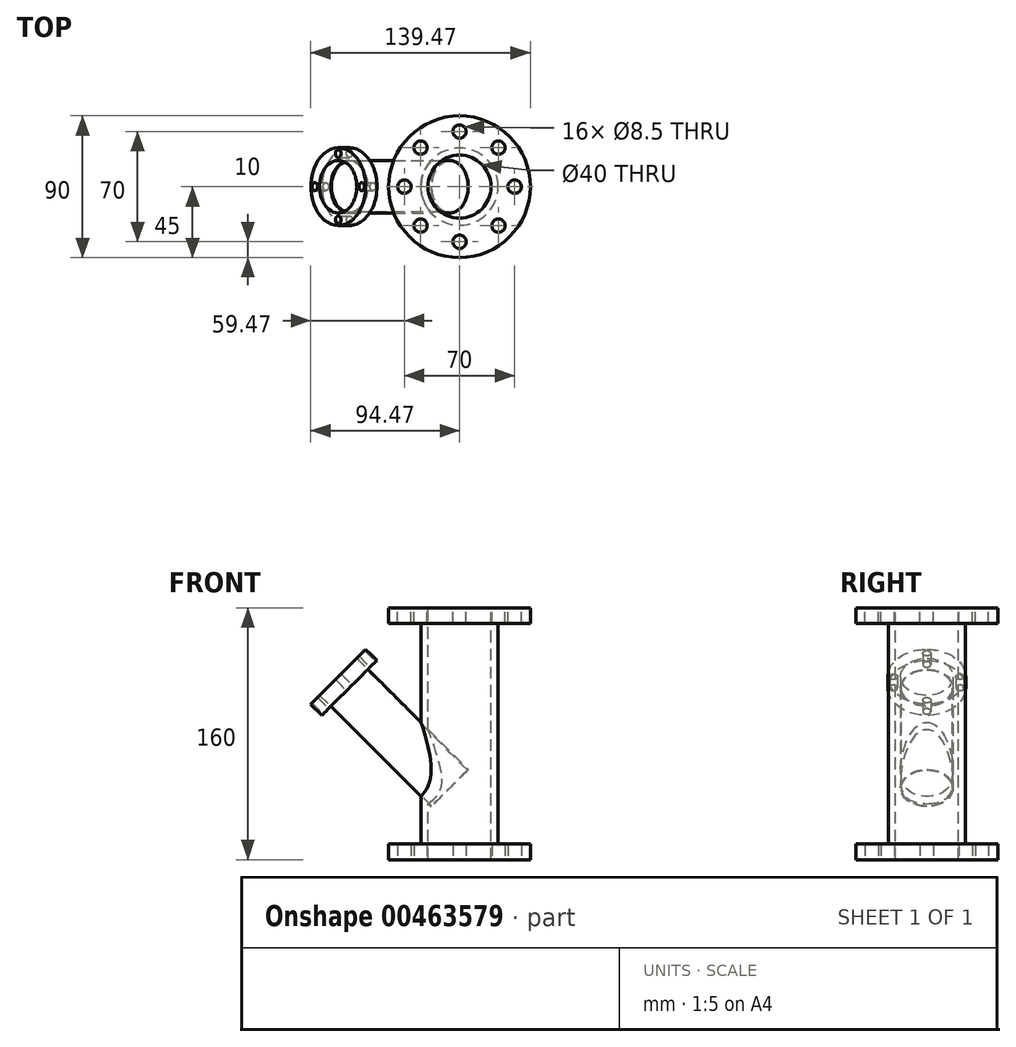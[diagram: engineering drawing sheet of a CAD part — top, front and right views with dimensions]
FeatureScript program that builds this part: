
annotation { "Feature Type Name" : "Feature", "Feature Type Description" : "" }
export const myFeature = defineFeature(function(context is Context, id is Id, definition is map)
    precondition{}
    {
        {
            var Q0;
            Q0=qCreatedBy(makeId("Top.planeOp"),FACE);
            var sketch = newSketch(context, id + "F0", { "sketchPlane" : qUnion([Q0])});
            skCircle(sketch, "E0", {"center": v(0, 0) * mm, "radius": 45 * mm});
            skSolve(sketch);
        }
        {
            var Q0;
            Q0=makeQuery(id+"F0.imprint","IMPRINT",FACE,{"disambiguationData":[TD([[makeQuery(id+"F0.imprint","IMPRINT",EDGE,{"derivedFrom":sQuery(id+"F0.wireOp",EDGE,"E0")}),1.0]])]});
            extrude(context, id + "F1", {"entities" : qUnion([Q0]), "depth" : 10 * mm});
        }
        {
            var Q0;
            Q0=makeQuery(id+"F1.opExtrude","CAP_FACE",FACE,{"disambiguationData":[OSD([sQuery(id+"F0.wireOp",EDGE,"E0")])],"isStart":true});
            var sketch = newSketch(context, id + "F2", { "sketchPlane" : qUnion([Q0])});
            skCircle(sketch, "E1", {"center": v(0, 0) * mm, "radius": 35 * mm});
            skCircle(sketch, "E2", {"center": v(0, 0) * mm, "radius": 20 * mm});
            skSolve(sketch);
        }
        {
            var Q0;
            Q0=makeQuery(id+"F1.opExtrude","CAP_FACE",FACE,{"disambiguationData":[OSD([sQuery(id+"F0.wireOp",EDGE,"E0")])],"isStart":false});
            var sketch = newSketch(context, id + "F3", { "sketchPlane" : qUnion([Q0])});
            skCircle(sketch, "E3", {"center": v(0, 0) * mm, "radius": 24.5 * mm});
            skSolve(sketch);
        }
        {
            var Q0;
            Q0=makeQuery(id+"F3.imprint","IMPRINT",FACE,{"disambiguationData":[TD([[makeQuery(id+"F3.imprint","IMPRINT",EDGE,{"derivedFrom":sQuery(id+"F3.wireOp",EDGE,"E3")}),1.0]])]});
            extrude(context, id + "F4", {"entities" : qUnion([Q0]), "operationType" : NewBodyOperationType.ADD, "depth" : 140 * mm});
        }
        {
            var Q0;
            Q0=makeQuery(id+"F4.opExtrude","CAP_FACE",FACE,{"disambiguationData":[OSD([sQuery(id+"F3.wireOp",EDGE,"E3")])],"isStart":false});
            var sketch = newSketch(context, id + "F5", { "sketchPlane" : qUnion([Q0])});
            skCircle(sketch, "E4", {"center": v(0, 0) * mm, "radius": 45 * mm});
            skSolve(sketch);
        }
        {
            var Q0;
            Q0=makeQuery(id+"F5.imprint","IMPRINT",FACE,{"disambiguationData":[TD([[makeQuery(id+"F5.imprint","IMPRINT",EDGE,{"derivedFrom":sQuery(id+"F5.wireOp",EDGE,"E4")}),1.0]])]});
            var Q1;
            Q1=makeQuery(id+"F5.imprint","IMPRINT",FACE,{"disambiguationData":[TD([[makeQuery(id+"F5.imprint","IMPRINT",EDGE,{"derivedFrom":makeQuery(id+"F4.opExtrude","CAP_EDGE",EDGE,{"disambiguationData":[OSD([sQuery(id+"F3.wireOp",EDGE,"E3")])],"isStart":false})}),1.0]])]});
            extrude(context, id + "F6", {"entities" : qUnion([Q0, Q1]), "operationType" : NewBodyOperationType.ADD, "depth" : 10 * mm});
        }
        {
            var Q0;
            Q0=makeQuery(id+"F6.opExtrude","CAP_FACE",FACE,{"disambiguationData":[OSD([sQuery(id+"F5.wireOp",EDGE,"E4")])],"isStart":false});
            var sketch = newSketch(context, id + "F7", { "sketchPlane" : qUnion([Q0])});
            skCircle(sketch, "E5", {"center": v(0, 0) * mm, "radius": 20 * mm});
            skCircle(sketch, "E6", {"center": v(0, 0) * mm, "radius": 35 * mm});
            skSolve(sketch);
        }
        {
            var Q0;
            Q0=makeQuery(id+"F7.imprint","IMPRINT",FACE,{"disambiguationData":[TD([[makeQuery(id+"F7.imprint","IMPRINT",EDGE,{"derivedFrom":sQuery(id+"F7.wireOp",EDGE,"E5")}),1.0]])]});
            extrude(context, id + "F8", {"entities" : qUnion([Q0]), "operationType" : NewBodyOperationType.REMOVE, "oppositeDirection" : true, "depth" : 500 * mm});
        }
        {
            var Q0;
            Q0=makeQuery(id+"F2.imprint","IMPRINT",FACE,{"disambiguationData":[TD([[makeQuery(id+"F2.imprint","IMPRINT",EDGE,{"derivedFrom":sQuery(id+"F2.wireOp",EDGE,"E1")}),-1.0]])]});
            var sketch = newSketch(context, id + "F9", { "sketchPlane" : qUnion([Q0])});
            skLineSegment(sketch, "E7", {"start": v(0, 0) * mm, "end": v(0, 30.75) * mm});
            skLineSegment(sketch, "E8", {"start": v(0, 75.16) * mm, "end": v(0, 39.25) * mm});
            skLineSegment(sketch, "E9", {"start": v(0, 0) * mm, "end": v(30.75, 0) * mm});
            skLineSegment(sketch, "E10", {"start": v(92.22, 0) * mm, "end": v(39.25, 0) * mm});
            skLineSegment(sketch, "E11", {"start": v(0, 0) * mm, "end": v(21.74, 21.74) * mm});
            skLineSegment(sketch, "E12", {"start": v(58.34, 58.34) * mm, "end": v(27.75, 27.75) * mm});
            skLineSegment(sketch, "E13", {"start": v(0, 0) * mm, "end": v(-60.15, 60.15) * mm});
            skLineSegment(sketch, "E14", {"start": v(-60.15, 60.15) * mm, "end": v(-27.75, 27.75) * mm});
            skArc(sketch, "E15", {"start": v(-27.57, 21.57) * mm, "mid": v(-32.34, 13.4) * mm, "end": v(-34.74, 4.24) * mm});
            skCircle(sketch, "E16", {"center": v(35, 0) * mm, "radius": 4.25 * mm});
            skCircle(sketch, "E17", {"center": v(24.75, 24.75) * mm, "radius": 4.25 * mm});
            skCircle(sketch, "E18", {"center": v(0, 35) * mm, "radius": 4.25 * mm});
            skCircle(sketch, "E19", {"center": v(24.75, -24.75) * mm, "radius": 4.25 * mm});
            skCircle(sketch, "E20", {"center": v(0, -35) * mm, "radius": 4.25 * mm});
            skCircle(sketch, "E21", {"center": v(-24.75, -24.75) * mm, "radius": 4.25 * mm});
            skCircle(sketch, "E22", {"center": v(-35, 0) * mm, "radius": 4.25 * mm});
            skCircle(sketch, "E23", {"center": v(-24.75, 24.75) * mm, "radius": 4.25 * mm});
            skLineSegment(sketch, "E24.trimOffspring", {"start": v(-21.74, 21.74) * mm, "end": v(21.74, -21.74) * mm});
            skLineSegment(sketch, "E25.trimOffspring", {"start": v(0, 30.75) * mm, "end": v(0, -30.75) * mm});
            skLineSegment(sketch, "E26.trimOffspring", {"start": v(0, 39.25) * mm, "end": v(0, 75.16) * mm});
            skArc(sketch, "E27.trimOffspring", {"start": v(21.57, 27.57) * mm, "mid": v(13.4, 32.34) * mm, "end": v(4.24, 34.74) * mm});
            skLineSegment(sketch, "E28.trimOffspring", {"start": v(21.74, 21.74) * mm, "end": v(0, 0) * mm});
            skLineSegment(sketch, "E29.trimOffspring", {"start": v(27.75, 27.75) * mm, "end": v(58.34, 58.34) * mm});
            skLineSegment(sketch, "E30.trimOffspring", {"start": v(30.75, 0) * mm, "end": v(0, 0) * mm});
            skLineSegment(sketch, "E31.trimOffspring", {"start": v(39.25, 0) * mm, "end": v(92.22, 0) * mm});
            skArc(sketch, "E32.trimOffspring", {"start": v(34.74, 4.24) * mm, "mid": v(32.34, 13.4) * mm, "end": v(27.57, 21.57) * mm});
            skLineSegment(sketch, "E33.trimOffspring", {"start": v(27.75, -27.75) * mm, "end": v(66.62, -66.62) * mm});
            skArc(sketch, "E34.trimOffspring", {"start": v(27.57, -21.57) * mm, "mid": v(32.34, -13.4) * mm, "end": v(34.74, -4.24) * mm});
            skArc(sketch, "E35.trimOffspring", {"start": v(4.24, -34.74) * mm, "mid": v(13.4, -32.34) * mm, "end": v(21.57, -27.57) * mm});
            skLineSegment(sketch, "E36.trimOffspring", {"start": v(0, -39.25) * mm, "end": v(0, -74.56) * mm});
            skArc(sketch, "E37.trimOffspring", {"start": v(-21.57, -27.57) * mm, "mid": v(-13.4, -32.34) * mm, "end": v(-4.24, -34.74) * mm});
            skLineSegment(sketch, "E38.trimOffspring", {"start": v(-27.75, -27.75) * mm, "end": v(-65.53, -65.53) * mm});
            skArc(sketch, "E39.trimOffspring", {"start": v(-34.74, -4.24) * mm, "mid": v(-32.34, -13.4) * mm, "end": v(-27.57, -21.57) * mm});
            skLineSegment(sketch, "E40.trimOffspring", {"start": v(-39.25, 0) * mm, "end": v(-107.6, 0) * mm});
            skSolve(sketch);
        }
        {
            var Q0;
            Q0=sQuery(id+"F9.wireOp",VERTEX,"E18.center");
            var Q1;
            Q1=sQuery(id+"F9.wireOp",VERTEX,"E17.center");
            var Q2;
            Q2=sQuery(id+"F9.wireOp",VERTEX,"E16.center");
            var Q3;
            Q3=sQuery(id+"F9.wireOp",VERTEX,"E19.center");
            var Q4;
            Q4=sQuery(id+"F9.wireOp",VERTEX,"E20.center");
            var Q5;
            Q5=sQuery(id+"F9.wireOp",VERTEX,"E21.center");
            var Q6;
            Q6=sQuery(id+"F9.wireOp",VERTEX,"E22.center");
            var Q7;
            Q7=sQuery(id+"F9.wireOp",VERTEX,"E23.center");
            var Q8;
            Q8=makeQuery(id+"F1.opExtrude","SWEPT_BODY",BODY,{"disambiguationData":[OSD([sQuery(id+"F0.wireOp",EDGE,"E0")])]});
            hole(context, id + "F10", {"style" : HoleStyle.SIMPLE, "endStyle" : HoleEndStyle.BLIND, "holeDiameter" : 8.5 * mm, "holeDepth" : 11 * mm, "isTappedThrough" : true, "tappedDepth" : 12 * mm, "tapClearance" : 3, "startFromSketch" : true, "locations" : qUnion([Q0, Q1, Q2, Q3, Q4, Q5, Q6, Q7]), "scope" : qUnion([Q8])});
        }
        {
            var Q0;
            Q0=makeQuery(id+"F6.opExtrude","CAP_FACE",FACE,{"disambiguationData":[OSD([sQuery(id+"F5.wireOp",EDGE,"E4")])],"isStart":false});
            var sketch = newSketch(context, id + "F11", { "sketchPlane" : qUnion([Q0])});
            skLineSegment(sketch, "E41", {"start": v(0, 0) * mm, "end": v(0, 45) * mm});
            skLineSegment(sketch, "E42", {"start": v(0, 45) * mm, "end": v(0, -45) * mm});
            skLineSegment(sketch, "E43", {"start": v(0, 0) * mm, "end": v(45, 0) * mm});
            skLineSegment(sketch, "E44", {"start": v(0, 0) * mm, "end": v(-45, 0) * mm});
            skLineSegment(sketch, "E45", {"start": v(0, 0) * mm, "end": v(45.49, 45.49) * mm});
            skLineSegment(sketch, "E46", {"start": v(0, 0) * mm, "end": v(-38.13, 38.13) * mm});
            skLineSegment(sketch, "E47", {"start": v(-38.13, 38.13) * mm, "end": v(51.85, -51.85) * mm});
            skLineSegment(sketch, "E48", {"start": v(45.49, 45.49) * mm, "end": v(-48.36, -48.36) * mm});
            skCircle(sketch, "E49", {"center": v(0, 0) * mm, "radius": 35 * mm});
            skCircle(sketch, "E50", {"center": v(-24.75, 24.75) * mm, "radius": 7.46 * mm});
            skCircle(sketch, "E51", {"center": v(0, 35) * mm, "radius": 6.7 * mm});
            skCircle(sketch, "E52", {"center": v(24.75, 24.75) * mm, "radius": 4.32 * mm});
            skCircle(sketch, "E53", {"center": v(35, 0) * mm, "radius": 2.12 * mm});
            skCircle(sketch, "E54", {"center": v(24.75, -24.75) * mm, "radius": 4.97 * mm});
            skCircle(sketch, "E55", {"center": v(0, -35) * mm, "radius": 4.88 * mm});
            skCircle(sketch, "E56", {"center": v(-24.75, -24.75) * mm, "radius": 2.86 * mm});
            skCircle(sketch, "E57", {"center": v(-35, 0) * mm, "radius": 1.96 * mm});
            skSolve(sketch);
        }
        {
            var Q0;
            Q0=sQuery(id+"F11.wireOp",VERTEX,"E50.center");
            var Q1;
            Q1=sQuery(id+"F11.wireOp",VERTEX,"E51.center");
            var Q2;
            Q2=sQuery(id+"F11.wireOp",VERTEX,"E52.center");
            var Q3;
            Q3=sQuery(id+"F11.wireOp",VERTEX,"E53.center");
            var Q4;
            Q4=sQuery(id+"F11.wireOp",VERTEX,"E54.center");
            var Q5;
            Q5=sQuery(id+"F11.wireOp",VERTEX,"E55.center");
            var Q6;
            Q6=sQuery(id+"F11.wireOp",VERTEX,"E56.center");
            var Q7;
            Q7=sQuery(id+"F11.wireOp",VERTEX,"E57.center");
            var Q8;
            Q8=makeQuery(id+"F1.opExtrude","SWEPT_BODY",BODY,{"disambiguationData":[OSD([sQuery(id+"F0.wireOp",EDGE,"E0")])]});
            hole(context, id + "F12", {"style" : HoleStyle.SIMPLE, "endStyle" : HoleEndStyle.BLIND, "holeDiameter" : 8.5 * mm, "holeDepth" : 11 * mm, "isTappedThrough" : true, "tappedDepth" : 12 * mm, "tapClearance" : 3, "startFromSketch" : true, "locations" : qUnion([Q0, Q1, Q2, Q3, Q4, Q5, Q6, Q7]), "scope" : qUnion([Q8])});
        }
        {
            var Q0;
            Q0=qCreatedBy(makeId("Front.planeOp"),FACE);
            var sketch = newSketch(context, id + "F13", { "sketchPlane" : qUnion([Q0])});
            skLineSegment(sketch, "E58", {"start": v(0, 0) * mm, "end": v(0, 120.53) * mm});
            skLineSegment(sketch, "E59", {"start": v(0, 0) * mm, "end": v(0, 40) * mm});
            skLineSegment(sketch, "E60", {"start": v(0, 40) * mm, "end": v(-75.44, 115.44) * mm});
            skSolve(sketch);
        }
        {
            var Q0;
            Q0=sQuery(id+"F13.wireOp",EDGE,"E60");
            cPlane(context, id + "F14", {"entities" : qUnion([Q0]), "cplaneType" : CPlaneType.MID_PLANE, "offset" : 25 * mm, "width" : 150 * mm, "height" : 150 * mm});
        }
        {
            var Q0;
            Q0=qCreatedBy(id+"F14.planeOp",FACE);
            var sketch = newSketch(context, id + "F15", { "sketchPlane" : qUnion([Q0])});
            skCircle(sketch, "E61", {"center": v(0, 27.71) * mm, "radius": 16.68 * mm});
            skSolve(sketch);
        }
        {
            var Q0;
            Q0=makeQuery(id+"F15.imprint","IMPRINT",FACE,{"disambiguationData":[TD([[makeQuery(id+"F15.imprint","IMPRINT",EDGE,{"derivedFrom":sQuery(id+"F15.wireOp",EDGE,"E61")}),1.0]])]});
            extrude(context, id + "F16", {"entities" : qUnion([Q0]), "operationType" : NewBodyOperationType.ADD, "endBound" : BoundingType.SYMMETRIC, "depth" : 90 * mm});
        }
        {
            var Q0;
            Q0=makeQuery(id+"F16.opExtrude","CAP_FACE",FACE,{"disambiguationData":[OSD([sQuery(id+"F15.wireOp",EDGE,"E61")])],"isStart":false});
            var sketch = newSketch(context, id + "F17", { "sketchPlane" : qUnion([Q0])});
            skCircle(sketch, "E62", {"center": v(0, 27.71) * mm, "radius": 24.68 * mm});
            skSolve(sketch);
        }
        {
            var Q0;
            Q0=makeQuery(id+"F17.imprint","IMPRINT",FACE,{"disambiguationData":[TD([[makeQuery(id+"F17.imprint","IMPRINT",EDGE,{"derivedFrom":sQuery(id+"F17.wireOp",EDGE,"E62")}),1.0]])]});
            extrude(context, id + "F18", {"entities" : qUnion([Q0]), "depth" : 10 * mm});
        }
        {
            var Q0;
            Q0=makeQuery(id+"F16.opExtrude","CAP_FACE",FACE,{"disambiguationData":[OSD([sQuery(id+"F15.wireOp",EDGE,"E61")])],"isStart":false});
            var sketch = newSketch(context, id + "F19", { "sketchPlane" : qUnion([Q0])});
            skLineSegment(sketch, "E63", {"start": v(0, 27.71) * mm, "end": v(0, 62.09) * mm});
            skLineSegment(sketch, "E64", {"start": v(0, 62.09) * mm, "end": v(0, -8.04) * mm});
            skLineSegment(sketch, "E65", {"start": v(0, -8.04) * mm, "end": v(0, 27.71) * mm});
            skLineSegment(sketch, "E66", {"start": v(0, 27.71) * mm, "end": v(48.35, 27.71) * mm});
            skLineSegment(sketch, "E67", {"start": v(0, 27.71) * mm, "end": v(-46.23, 27.71) * mm});
            skCircle(sketch, "E68", {"center": v(0, 27.71) * mm, "radius": 21.05 * mm});
            skCircle(sketch, "E69", {"center": v(0, 48.76) * mm, "radius": 2 * mm});
            skCircle(sketch, "E70", {"center": v(21.05, 27.71) * mm, "radius": 1.45 * mm});
            skCircle(sketch, "E71", {"center": v(-21.05, 27.71) * mm, "radius": 0.95 * mm});
            skCircle(sketch, "E72", {"center": v(0, 6.66) * mm, "radius": 3.43 * mm});
            skSolve(sketch);
        }
        {
            var Q0;
            Q0=sQuery(id+"F19.wireOp",VERTEX,"E69.center");
            var Q1;
            Q1=sQuery(id+"F19.wireOp",VERTEX,"E70.center");
            var Q2;
            Q2=sQuery(id+"F19.wireOp",VERTEX,"E72.center");
            var Q3;
            Q3=sQuery(id+"F19.wireOp",VERTEX,"E71.center");
            var Q4;
            Q4=makeQuery(id+"F18.opExtrude","SWEPT_BODY",BODY,{"disambiguationData":[OSD([sQuery(id+"F15.wireOp",EDGE,"E61"),sQuery(id+"F17.wireOp",EDGE,"E62")])]});
            hole(context, id + "F20", {"style" : HoleStyle.SIMPLE, "endStyle" : HoleEndStyle.BLIND, "oppositeDirection" : true, "holeDiameter" : 5 * mm, "holeDepth" : 11 * mm, "isTappedThrough" : true, "tappedDepth" : 12 * mm, "tapClearance" : 3, "startFromSketch" : true, "locations" : qUnion([Q0, Q1, Q2, Q3]), "scope" : qUnion([Q4])});
        }
        {
            var Q0;
            Q0=makeQuery(id+"F16.opExtrude","CAP_FACE",FACE,{"disambiguationData":[OSD([sQuery(id+"F15.wireOp",EDGE,"E61")])],"isStart":false});
            var sketch = newSketch(context, id + "F21", { "sketchPlane" : qUnion([Q0])});
            skCircle(sketch, "E73", {"center": v(0, 27.71) * mm, "radius": 16.14 * mm});
            skSolve(sketch);
        }
        {
            var Q0;
            Q0=makeQuery(id+"F21.imprint","IMPRINT",FACE,{"disambiguationData":[TD([[makeQuery(id+"F21.imprint","IMPRINT",EDGE,{"derivedFrom":sQuery(id+"F21.wireOp",EDGE,"E73")}),1.0]])]});
            extrude(context, id + "F22", {"entities" : qUnion([Q0]), "operationType" : NewBodyOperationType.REMOVE, "oppositeDirection" : true, "depth" : 90 * mm});
        }
    });
